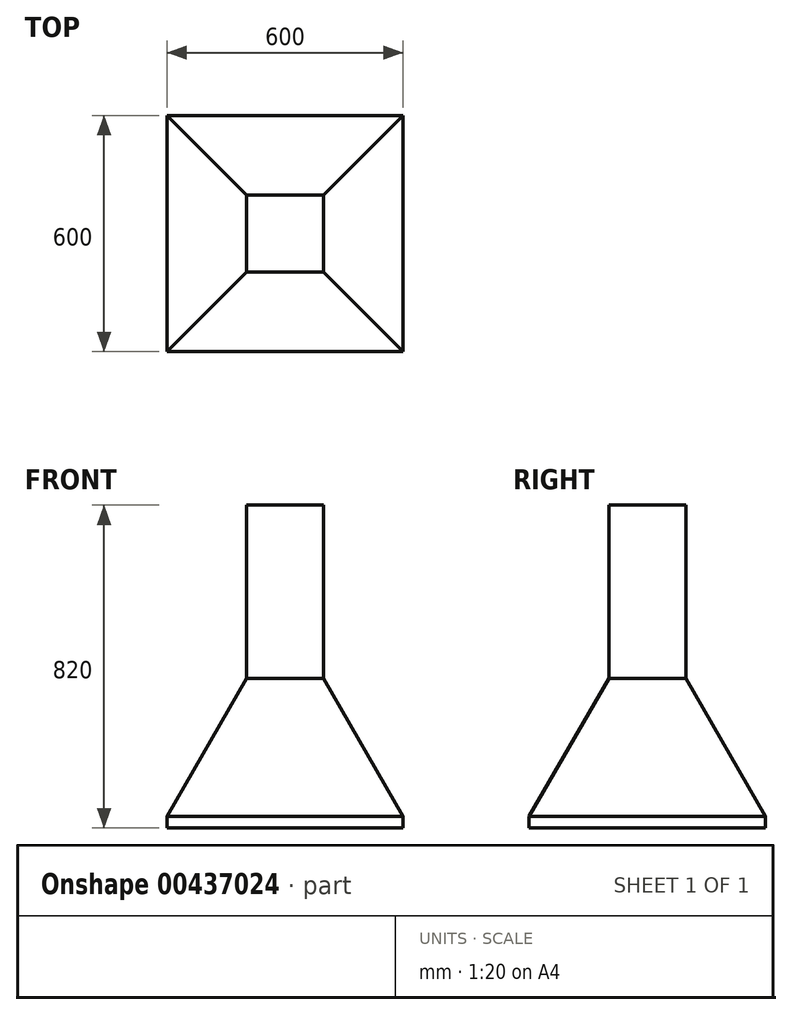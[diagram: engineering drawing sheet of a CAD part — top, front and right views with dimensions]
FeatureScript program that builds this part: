
annotation { "Feature Type Name" : "Feature", "Feature Type Description" : "" }
export const myFeature = defineFeature(function(context is Context, id is Id, definition is map)
    precondition{}
    {
        {
            var Q0;
            Q0=qCreatedBy(makeId("Top.planeOp"),FACE);
            var sketch = newSketch(context, id + "F0", { "sketchPlane" : qUnion([Q0])});
            skLineSegment(sketch, "E0.bottom", {"start": v(0, 0) * mm, "end": v(-600, 0) * mm});
            skLineSegment(sketch, "E0.top", {"start": v(0, 600) * mm, "end": v(-600, 600) * mm});
            skLineSegment(sketch, "E0.left", {"start": v(0, 0) * mm, "end": v(0, 600) * mm});
            skLineSegment(sketch, "E0.right", {"start": v(-600, 0) * mm, "end": v(-600, 600) * mm});
            skSolve(sketch);
        }
        {
            var Q0;
            Q0 = qSketchRegion(id + "F0", true);
            extrude(context, id + "F1", {"entities" : qUnion([Q0]), "depth" : 380 * mm});
        }
        {
            var Q0;
            Q0=makeQuery(id+"F1.opExtrude","CAP_FACE",FACE,{"disambiguationData":[OSD([sQuery(id+"F0.wireOp",EDGE,"E0.bottom"),sQuery(id+"F0.wireOp",EDGE,"E0.top"),sQuery(id+"F0.wireOp",EDGE,"E0.left"),sQuery(id+"F0.wireOp",EDGE,"E0.right")])],"isStart":false});
            chamfer(context, id + "F2", {"entities" : qUnion([Q0]), "chamferType" : ChamferType.OFFSET_ANGLE, "width" : 350 * mm, "oppositeDirection" : false, "angle" : 30 * degree, "tangentPropagation" : true});
        }
        {
            var Q0;
            Q0=makeQuery(id+"F1.opExtrude","CAP_FACE",FACE,{"disambiguationData":[OSD([sQuery(id+"F0.wireOp",EDGE,"E0.bottom"),sQuery(id+"F0.wireOp",EDGE,"E0.top"),sQuery(id+"F0.wireOp",EDGE,"E0.left"),sQuery(id+"F0.wireOp",EDGE,"E0.right")])],"isStart":false});
            var sketch = newSketch(context, id + "F3", { "sketchPlane" : qUnion([Q0])});
            skSolve(sketch);
        }
        {
            var Q0;
            Q0 = qSketchRegion(id + "F3", true);
            var Q1;
            {var subQ0=sQuery(id+"F0.wireOp",EDGE,"E0.right");var subQ1=sQuery(id+"F0.wireOp",EDGE,"E0.left");var subQ2=sQuery(id+"F0.wireOp",EDGE,"E0.top");var subQ3=sQuery(id+"F0.wireOp",EDGE,"E0.bottom");var subQ4=makeQuery(id+"F1.opExtrude","CAP_FACE",FACE,{"disambiguationData":[OSD([subQ3,subQ2,subQ1,subQ0])],"isStart":false});Q1=makeQuery(id+"F3.imprint","IMPRINT",FACE,{"disambiguationData":[TD([[makeQuery(id+"F3.imprint","IMPRINT",EDGE,{"derivedFrom":makeQuery(id+"F2.opChamfer","BLEND_EDGE",EDGE,{"blendedFrom":[makeQuery(id+"F1.opExtrude","CAP_EDGE",EDGE,{"disambiguationData":[OSD([subQ3])],"isStart":false}),subQ4],"blendedInto":[subQ4]})}),1.0]])]});}
            extrude(context, id + "F4", {"entities" : qUnion([Q0, Q1]), "operationType" : NewBodyOperationType.ADD, "depth" : 440 * mm});
        }
    });
